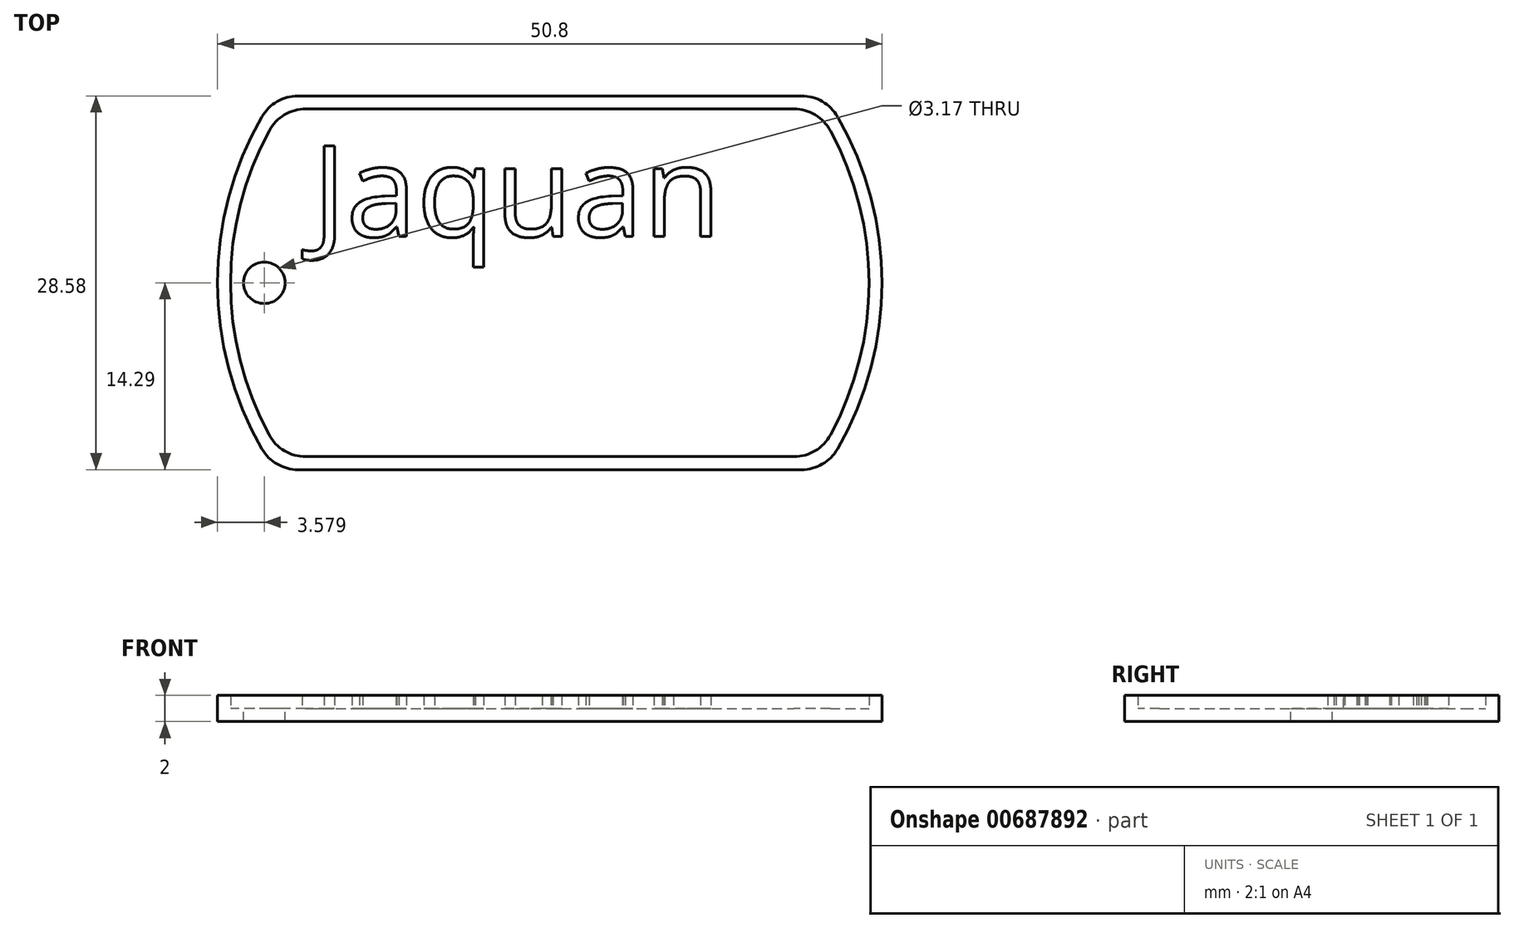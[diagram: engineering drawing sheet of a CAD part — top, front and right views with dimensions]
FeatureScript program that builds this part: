
annotation { "Feature Type Name" : "Feature", "Feature Type Description" : "" }
export const myFeature = defineFeature(function(context is Context, id is Id, definition is map)
    precondition{}
    {
        {
            var Q0;
            Q0=qCreatedBy(makeId("Top.planeOp"),FACE);
            var sketch = newSketch(context, id + "F0", { "sketchPlane" : qUnion([Q0])});
            skArc(sketch, "E0", {"start": v(-22, 12.7) * mm, "mid": v(-25.4, 0) * mm, "end": v(-22, -12.7) * mm});
            skLineSegment(sketch, "E1.top", {"start": v(-19.25, -14.29) * mm, "end": v(19.25, -14.29) * mm});
            skArc(sketch, "E2.trimOffspring", {"start": v(22, -12.7) * mm, "mid": v(25.4, 0) * mm, "end": v(22, 12.7) * mm});
            skLineSegment(sketch, "E3", {"start": v(-19.25, 14.29) * mm, "end": v(19.25, 14.29) * mm});
            skPoint(sketch, "E4.visualSharp", {"position": v(-21, 14.29) * mm});
            skArc(sketch, "E4.filletArc", {"start": v(-19.25, 14.29) * mm, "mid": v(-20.83, 13.86) * mm, "end": v(-22, 12.7) * mm});
            skPoint(sketch, "E5.visualSharp", {"position": v(21, 14.29) * mm});
            skArc(sketch, "E5.filletArc", {"start": v(22, 12.7) * mm, "mid": v(20.83, 13.86) * mm, "end": v(19.25, 14.29) * mm});
            skPoint(sketch, "E6.visualSharp", {"position": v(21, -14.29) * mm});
            skArc(sketch, "E6.filletArc", {"start": v(19.25, -14.29) * mm, "mid": v(20.83, -13.86) * mm, "end": v(22, -12.7) * mm});
            skPoint(sketch, "E7.visualSharp", {"position": v(-21, -14.29) * mm});
            skArc(sketch, "E7.filletArc", {"start": v(-22, -12.7) * mm, "mid": v(-20.83, -13.86) * mm, "end": v(-19.25, -14.29) * mm});
            skSolve(sketch);
        }
        {
            var Q0;
            Q0=makeQuery(id+"F0.imprint","IMPRINT",FACE,{"disambiguationData":[TD([[makeQuery(id+"F0.imprint","IMPRINT",EDGE,{"derivedFrom":sQuery(id+"F0.wireOp",EDGE,"E0")}),1.0]])]});
            extrude(context, id + "F1", {"entities" : qUnion([Q0]), "depth" : 1 * mm, "offsetDistance" : 25.4 * mm});
        }
        {
            var Q0;
            Q0=makeQuery(id+"F1.opExtrude","CAP_FACE",FACE,{"disambiguationData":[OSD([sQuery(id+"F0.wireOp",EDGE,"E0"),sQuery(id+"F0.wireOp",EDGE,"E1.top"),sQuery(id+"F0.wireOp",EDGE,"E2.trimOffspring"),sQuery(id+"F0.wireOp",EDGE,"E3"),sQuery(id+"F0.wireOp",EDGE,"E4.filletArc"),sQuery(id+"F0.wireOp",EDGE,"E5.filletArc"),sQuery(id+"F0.wireOp",EDGE,"E6.filletArc"),sQuery(id+"F0.wireOp",EDGE,"E7.filletArc")])],"isStart":false});
            var sketch = newSketch(context, id + "F2", { "sketchPlane" : qUnion([Q0])});
            skLineSegment(sketch, "E8.0", {"start": v(-18.66, 13.29) * mm, "end": v(18.66, 13.29) * mm});
            skArc(sketch, "E8.1", {"start": v(-21.45, 11.63) * mm, "mid": v(-24.4, 0) * mm, "end": v(-21.45, -11.63) * mm});
            skLineSegment(sketch, "E8.2", {"start": v(-18.66, -13.29) * mm, "end": v(18.66, -13.29) * mm});
            skArc(sketch, "E8.3", {"start": v(21.45, -11.63) * mm, "mid": v(24.4, 0) * mm, "end": v(21.45, 11.63) * mm});
            skPoint(sketch, "E9.visualSharp", {"position": v(-20.46, 13.29) * mm});
            skArc(sketch, "E9.filletArc", {"start": v(-18.66, 13.29) * mm, "mid": v(-20.29, 12.84) * mm, "end": v(-21.45, 11.63) * mm});
            skPoint(sketch, "E10.visualSharp", {"position": v(20.46, 13.29) * mm});
            skArc(sketch, "E10.filletArc", {"start": v(21.45, 11.63) * mm, "mid": v(20.29, 12.84) * mm, "end": v(18.66, 13.29) * mm});
            skPoint(sketch, "E11.visualSharp", {"position": v(20.46, -13.29) * mm});
            skArc(sketch, "E11.filletArc", {"start": v(18.66, -13.29) * mm, "mid": v(20.29, -12.84) * mm, "end": v(21.45, -11.63) * mm});
            skPoint(sketch, "E12.visualSharp", {"position": v(-20.46, -13.29) * mm});
            skArc(sketch, "E12.filletArc", {"start": v(-21.45, -11.63) * mm, "mid": v(-20.29, -12.84) * mm, "end": v(-18.66, -13.29) * mm});
            skLineSegment(sketch, "E13.0", {"start": v(-19.25, 14.29) * mm, "end": v(19.25, 14.29) * mm});
            skArc(sketch, "E13.1", {"start": v(-22, 12.7) * mm, "mid": v(-25.4, 0) * mm, "end": v(-22, -12.7) * mm});
            skLineSegment(sketch, "E13.2", {"start": v(-19.25, -14.29) * mm, "end": v(19.25, -14.29) * mm});
            skArc(sketch, "E13.3", {"start": v(22, -12.7) * mm, "mid": v(25.4, 0) * mm, "end": v(22, 12.7) * mm});
            skPoint(sketch, "E14.visualSharp", {"position": v(-21, -14.29) * mm});
            skArc(sketch, "E14.filletArc", {"start": v(-22, -12.7) * mm, "mid": v(-20.83, -13.86) * mm, "end": v(-19.25, -14.29) * mm});
            skPoint(sketch, "E15.visualSharp", {"position": v(21, -14.29) * mm});
            skArc(sketch, "E15.filletArc", {"start": v(19.25, -14.29) * mm, "mid": v(20.83, -13.86) * mm, "end": v(22, -12.7) * mm});
            skPoint(sketch, "E16.visualSharp", {"position": v(21, 14.29) * mm});
            skArc(sketch, "E16.filletArc", {"start": v(22, 12.7) * mm, "mid": v(20.83, 13.86) * mm, "end": v(19.25, 14.29) * mm});
            skPoint(sketch, "E17.visualSharp", {"position": v(-21, 14.29) * mm});
            skArc(sketch, "E17.filletArc", {"start": v(-19.25, 14.29) * mm, "mid": v(-20.83, 13.86) * mm, "end": v(-22, 12.7) * mm});
            skSolve(sketch);
        }
        {
            var Q0;
            Q0=makeQuery(id+"F2.imprint","IMPRINT",FACE,{"disambiguationData":[TD([[makeQuery(id+"F2.imprint","IMPRINT",EDGE,{"derivedFrom":sQuery(id+"F2.wireOp",EDGE,"E8.0")}),1.0]])]});
            extrude(context, id + "F3", {"entities" : qUnion([Q0]), "operationType" : NewBodyOperationType.ADD, "depth" : 1 * mm, "offsetDistance" : 25.4 * mm});
        }
        {
            var Q0;
            Q0=makeQuery(id+"F1.opExtrude","CAP_FACE",FACE,{"disambiguationData":[OSD([sQuery(id+"F0.wireOp",EDGE,"E0"),sQuery(id+"F0.wireOp",EDGE,"E1.top"),sQuery(id+"F0.wireOp",EDGE,"E2.trimOffspring"),sQuery(id+"F0.wireOp",EDGE,"E3"),sQuery(id+"F0.wireOp",EDGE,"E4.filletArc"),sQuery(id+"F0.wireOp",EDGE,"E5.filletArc"),sQuery(id+"F0.wireOp",EDGE,"E6.filletArc"),sQuery(id+"F0.wireOp",EDGE,"E7.filletArc")])],"isStart":false});
            var sketch = newSketch(context, id + "F4", { "sketchPlane" : qUnion([Q0])});
            skCircle(sketch, "E18", {"center": v(-21.82, 0) * mm, "radius": 1.59 * mm});
            skSolve(sketch);
        }
        {
            var Q0;
            Q0=makeQuery(id+"F4.imprint","IMPRINT",FACE,{"disambiguationData":[TD([[makeQuery(id+"F4.imprint","IMPRINT",EDGE,{"derivedFrom":sQuery(id+"F4.wireOp",EDGE,"E18")}),1.0]])]});
            extrude(context, id + "F5", {"entities" : qUnion([Q0]), "operationType" : NewBodyOperationType.REMOVE, "oppositeDirection" : true, "depth" : 1 * mm, "offsetDistance" : 25.4 * mm});
        }
        {
            var Q0;
            Q0=makeQuery(id+"F2.imprint","IMPRINT",FACE,{"disambiguationData":[TD([[makeQuery(id+"F2.imprint","IMPRINT",EDGE,{"derivedFrom":sQuery(id+"F2.wireOp",EDGE,"E8.0")}),-1.0]])]});
            var sketch = newSketch(context, id + "F6", { "sketchPlane" : qUnion([Q0])});
            skText(sketch, "E19", { "text": "Jaquan", "fontName": "OpenSans-Regular.ttf"});
            const initialGuessF6  = {"E19": [-0.01816, 0.00354, 1, 0, 0.00699]};
            skSetInitialGuess(sketch, initialGuessF6);
            skSolve(sketch);
        }
        {
            var Q0;
            Q0 = qSketchRegion(id + "F6", true);
            extrude(context, id + "F7", {"entities" : qUnion([Q0]), "operationType" : NewBodyOperationType.ADD, "depth" : 1 * mm, "offsetDistance" : 25.4 * mm});
        }
    });
